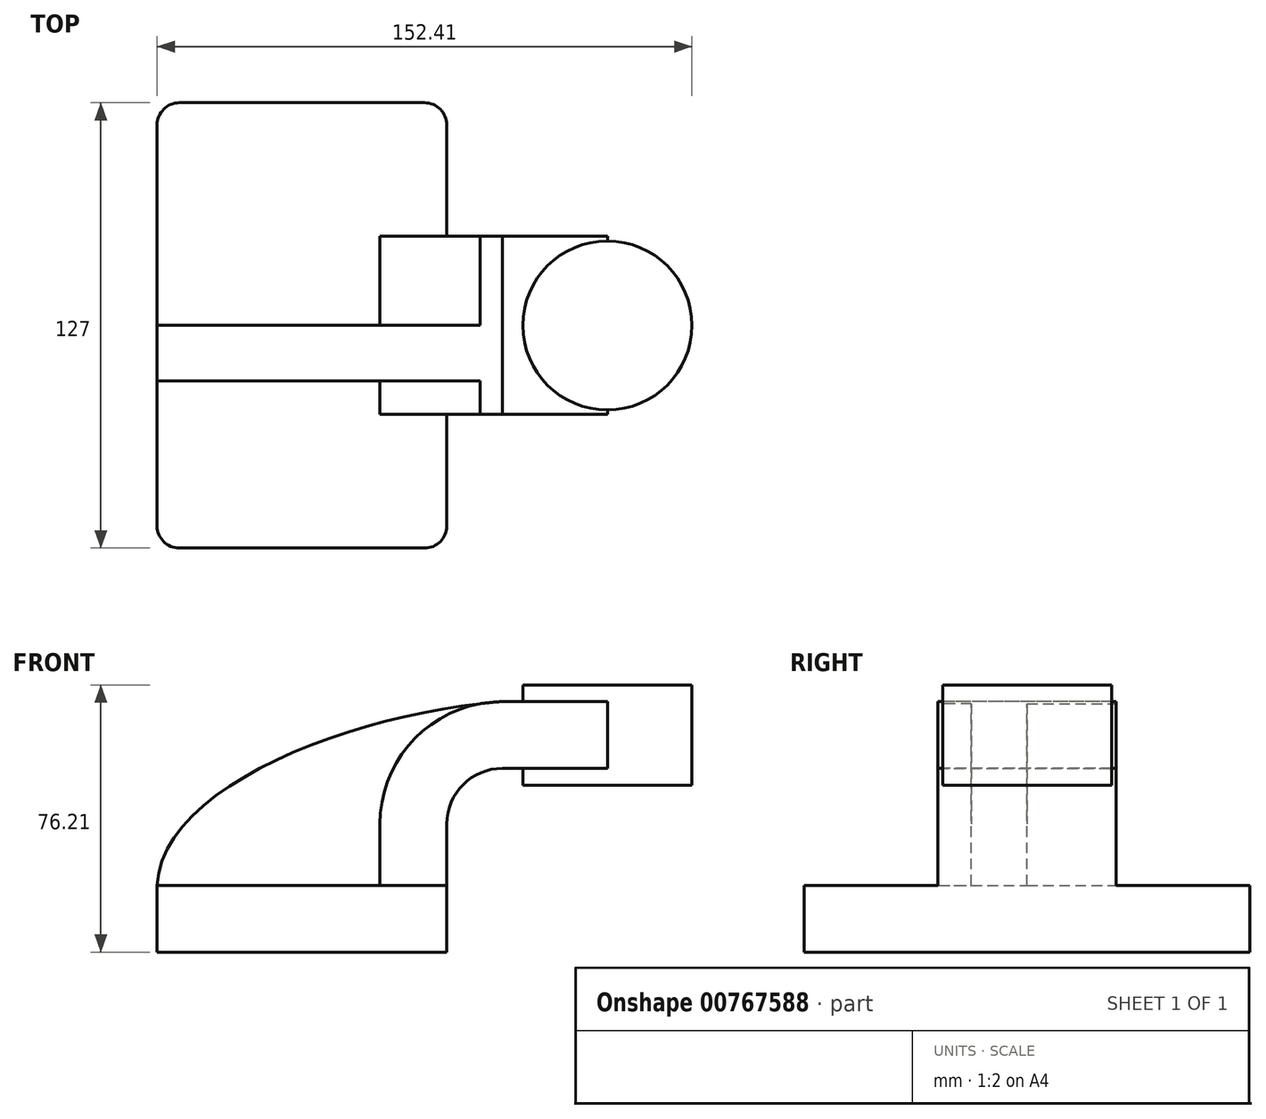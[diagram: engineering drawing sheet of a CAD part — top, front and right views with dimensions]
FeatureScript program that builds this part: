
annotation { "Feature Type Name" : "Feature", "Feature Type Description" : "" }
export const myFeature = defineFeature(function(context is Context, id is Id, definition is map)
    precondition{}
    {
        {
            var Q0;
            Q0=qCreatedBy(makeId("Front.planeOp"),FACE);
            var sketch = newSketch(context, id + "F0", { "sketchPlane" : qUnion([Q0])});
            skLineSegment(sketch, "E0.bottom", {"start": v(41.28, -9.52) * mm, "end": v(-41.28, -9.53) * mm});
            skLineSegment(sketch, "E0.top", {"start": v(41.28, 9.53) * mm, "end": v(-41.28, 9.53) * mm});
            skLineSegment(sketch, "E0.left", {"start": v(41.28, -9.52) * mm, "end": v(41.28, 9.53) * mm});
            skLineSegment(sketch, "E0.right", {"start": v(-41.28, -9.53) * mm, "end": v(-41.28, 9.53) * mm});
            skPoint(sketch, "E0.middle", {"position": v(0, 0) * mm});
            skLineSegment(sketch, "E1.bottom", {"start": v(111.12, 38.1) * mm, "end": v(60.32, 38.1) * mm});
            skLineSegment(sketch, "E1.top", {"start": v(111.12, 66.68) * mm, "end": v(60.32, 66.68) * mm});
            skLineSegment(sketch, "E1.left", {"start": v(111.12, 38.1) * mm, "end": v(111.12, 66.68) * mm});
            skLineSegment(sketch, "E1.right", {"start": v(60.32, 38.1) * mm, "end": v(60.32, 66.68) * mm});
            skPoint(sketch, "E1.middle", {"position": v(85.72, 52.39) * mm});
            skLineSegment(sketch, "E2", {"start": v(41.28, 9.53) * mm, "end": v(41.28, 27) * mm});
            skArc(sketch, "E3", {"start": v(41.27, 27) * mm, "mid": v(45.92, 38.23) * mm, "end": v(57.15, 42.88) * mm});
            skLineSegment(sketch, "E4", {"start": v(57.15, 42.88) * mm, "end": v(87.03, 42.88) * mm});
            skLineSegment(sketch, "E5.0", {"start": v(57.15, 61.93) * mm, "end": v(87.03, 61.93) * mm});
            skArc(sketch, "E5.1", {"start": v(22.23, 27) * mm, "mid": v(32.45, 51.7) * mm, "end": v(57.15, 61.93) * mm});
            skLineSegment(sketch, "E5.2", {"start": v(22.22, 9.53) * mm, "end": v(22.22, 27) * mm});
            skLineSegment(sketch, "E6", {"start": v(87.03, 66.68) * mm, "end": v(87.03, 38.1) * mm});
            skFitSpline(sketch, "E7", {"points": [v(-41.28, 9.52) * mm, v(57.15, 61.93) * mm], "startDerivative": vector(3.64, 86.88) * mm, "endDerivative": vector(121.12, 8.75) * mm});
            skSolve(sketch);
        }
        {
            var Q0;
            Q0=makeQuery(id+"F0.imprint","IMPRINT",FACE,{"disambiguationData":[TD([[makeQuery(id+"F0.imprint","IMPRINT",EDGE,{"derivedFrom":sQuery(id+"F0.wireOp",EDGE,"E0.bottom")}),-1.0]])]});
            extrude(context, id + "F1", {"entities" : qUnion([Q0]), "endBound" : BoundingType.SYMMETRIC, "depth" : 127 * mm, "offsetDistance" : 25.4 * mm});
        }
        {
            var Q0;
            {var subQ1=sQuery(id+"F0.wireOp",EDGE,"E2");Q0=makeQuery(id+"F0.imprint","IMPRINT",FACE,{"disambiguationData":[TD([[makeQuery(id+"F0.imprint","IMPRINT",EDGE,{"derivedFrom":subQ1}),1.0]])]});}
            var Q1;
            {var subQ0=sQuery(id+"F0.wireOp",EDGE,"E4");var subQ1=sQuery(id+"F0.wireOp",EDGE,"E1.right");var subQ2=makeQuery(id+"F0.imprint","INTERSECT",VERTEX,{"derivedFrom":[subQ1,subQ0]});Q1=makeQuery(id+"F0.imprint","IMPRINT",FACE,{"disambiguationData":[TD([[makeQuery(id+"F0.imprint","IMPRINT",EDGE,{"disambiguationData":[TD([[subQ2,-1.0]])],"derivedFrom":subQ1}),-1.0]])]});}
            extrude(context, id + "F2", {"entities" : qUnion([Q0, Q1]), "operationType" : NewBodyOperationType.ADD, "endBound" : BoundingType.SYMMETRIC, "depth" : 50.8 * mm, "offsetDistance" : 25.4 * mm});
        }
        {
            var Q0;
            {var subQ3=sQuery(id+"F0.wireOp",EDGE,"E5.2");Q0=makeQuery(id+"F0.imprint","IMPRINT",FACE,{"disambiguationData":[TD([[makeQuery(id+"F0.imprint","IMPRINT",EDGE,{"derivedFrom":subQ3}),1.0]])]});}
            extrude(context, id + "F3", {"entities" : qUnion([Q0]), "operationType" : NewBodyOperationType.ADD, "depth" : 15.88 * mm, "offsetDistance" : 25.4 * mm});
        }
        {
            var Q0;
            {var subQ0=sQuery(id+"F0.wireOp",EDGE,"E1.left");Q0=makeQuery(id+"F0.imprint","IMPRINT",FACE,{"disambiguationData":[TD([[makeQuery(id+"F0.imprint","IMPRINT",EDGE,{"derivedFrom":subQ0}),1.0]])]});}
            var Q1;
            Q1=sQuery(id+"F0.wireOp",EDGE,"E6");
            revolve(context, id + "F4", {"operationType" : NewBodyOperationType.ADD, "surfaceOperationType" : NewSurfaceOperationType.NEW, "entities" : qUnion([Q0]), "axis" : qUnion([Q1]), "revolveType" : RevolveType.FULL});
        }
        {
            var Q0;
            Q0=makeQuery(id+"F1.opExtrude","CAP_EDGE",EDGE,{"disambiguationData":[OSD([sQuery(id+"F0.wireOp",EDGE,"E0.left")])],"isStart":false});
            var Q1;
            Q1=makeQuery(id+"F1.opExtrude","CAP_EDGE",EDGE,{"disambiguationData":[OSD([sQuery(id+"F0.wireOp",EDGE,"E0.right")])],"isStart":false});
            var Q2;
            Q2=makeQuery(id+"F1.opExtrude","CAP_EDGE",EDGE,{"disambiguationData":[OSD([sQuery(id+"F0.wireOp",EDGE,"E0.left")])],"isStart":true});
            var Q3;
            Q3=makeQuery(id+"F1.opExtrude","CAP_EDGE",EDGE,{"disambiguationData":[OSD([sQuery(id+"F0.wireOp",EDGE,"E0.right")])],"isStart":true});
            fillet(context, id + "F5", {"entities" : qUnion([Q0, Q1, Q2, Q3]), "radius" : 6.35 * mm, "tangentPropagation" : true, "allowEdgeOverflow" : false});
        }
    });
